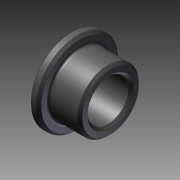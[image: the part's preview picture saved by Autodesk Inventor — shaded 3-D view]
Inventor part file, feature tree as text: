
AUTODESK INVENTOR PART (.ipt)
format: ipt  version: 2015 SP1 (Build 190203100, 203)  size: 129,024 bytes
history: native  units: mm
features: revolve x1, sketch x1
ambient origin geometry x8: Origin, YZ Plane, XZ Plane, XY Plane, X Axis, Y Axis, Z Axis, Center Point
bodies: Solid1 (feature_tree)
feature tree (2):
  revolve  "Revolution1"  [1 undecoded]
  sketch  "Skizze_1"  dims[d0=360.0deg]
note: 1 required parameter value undecoded (feature->parameter linkage not recoverable at this tier; creation-order binding heuristic only, values carry confidence <= 0.55)
